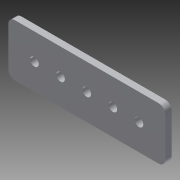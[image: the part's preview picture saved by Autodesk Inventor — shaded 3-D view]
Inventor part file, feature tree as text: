
AUTODESK INVENTOR PART (.ipt)
format: ipt  version: 2014 (Build 180170000, 170)  size: 93,184 bytes
history: native  units: in
note: dims shown in document units (in); Inventor stores cm internally (conversion verified against a paired STEP export)
features: extrude x1, fillet x1, sketch x1
ambient origin geometry x8: Origin, YZ Plane, XZ Plane, XY Plane, X Axis, Y Axis, Z Axis, Center Point
bodies: Solid1 (feature_tree)
feature tree (3):
  extrude  "Extrusion1"  Depth=1.0in
  fillet  "Fillet1"  Radius=0.164in
  sketch  "Sketch1"  dims[d0=3.0in d1=1.0in d2=0.164in d3=0.5in d4=0.5in d5=1.9685in d7=0.5in d8=0.3937in d10=1.0in d12=0.125in d13=0.0in d14=0.125in]
